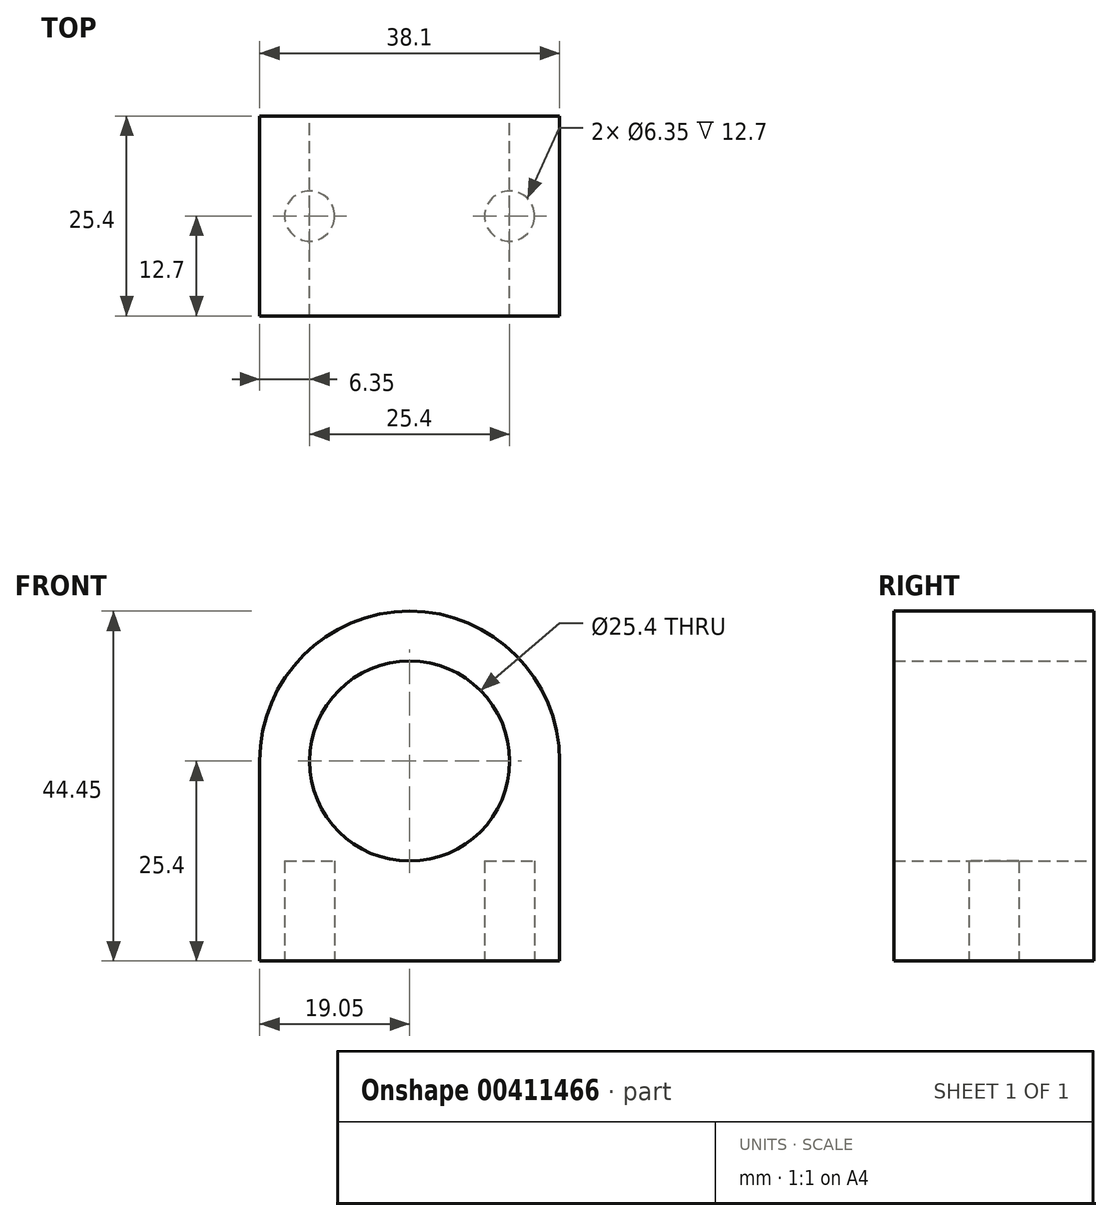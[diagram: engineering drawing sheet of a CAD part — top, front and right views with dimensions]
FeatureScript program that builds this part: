
annotation { "Feature Type Name" : "Feature", "Feature Type Description" : "" }
export const myFeature = defineFeature(function(context is Context, id is Id, definition is map)
    precondition{}
    {
        {
            var Q0;
            Q0=qCreatedBy(makeId("Front.planeOp"),FACE);
            var sketch = newSketch(context, id + "F0", { "sketchPlane" : qUnion([Q0])});
            skLineSegment(sketch, "E0.top", {"start": v(-19.05, -12.7) * mm, "end": v(19.05, -12.7) * mm});
            skLineSegment(sketch, "E0.left", {"start": v(-19.05, 12.7) * mm, "end": v(-19.05, -12.7) * mm});
            skLineSegment(sketch, "E0.right", {"start": v(19.05, 12.7) * mm, "end": v(19.05, -12.7) * mm});
            skArc(sketch, "E1", {"start": v(19.05, 12.7) * mm, "mid": v(0, 31.75) * mm, "end": v(-19.05, 12.7) * mm});
            skCircle(sketch, "E2", {"center": v(0, 12.7) * mm, "radius": 12.7 * mm});
            skSolve(sketch);
        }
        {
            var Q0;
            Q0=makeQuery(id+"F0.imprint","IMPRINT",FACE,{"disambiguationData":[TD([[makeQuery(id+"F0.imprint","IMPRINT",EDGE,{"derivedFrom":sQuery(id+"F0.wireOp",EDGE,"E0.top")}),1.0]])]});
            extrude(context, id + "F1", {"entities" : qUnion([Q0]), "depth" : 25.4 * mm});
        }
        {
            var Q0;
            Q0=makeQuery(id+"F1.opExtrude","SWEPT_FACE",FACE,{"disambiguationData":[OSD([sQuery(id+"F0.wireOp",EDGE,"E0.top")])]});
            var sketch = newSketch(context, id + "F2", { "sketchPlane" : qUnion([Q0])});
            skCircle(sketch, "E3", {"center": v(-12.7, 12.7) * mm, "radius": 3.18 * mm});
            skPoint(sketch, "E3.centerSnap0", {"position": v(-19.05, 12.7) * mm});
            skCircle(sketch, "E4", {"center": v(12.7, 12.7) * mm, "radius": 3.18 * mm});
            skSolve(sketch);
        }
        {
            var Q0;
            Q0=makeQuery(id+"F2.imprint","IMPRINT",FACE,{"disambiguationData":[TD([[makeQuery(id+"F2.imprint","IMPRINT",EDGE,{"derivedFrom":sQuery(id+"F2.wireOp",EDGE,"E3")}),1.0]])]});
            var Q1;
            Q1=makeQuery(id+"F2.imprint","IMPRINT",FACE,{"disambiguationData":[TD([[makeQuery(id+"F2.imprint","IMPRINT",EDGE,{"derivedFrom":sQuery(id+"F2.wireOp",EDGE,"E4")}),1.0]])]});
            extrude(context, id + "F3", {"entities" : qUnion([Q0, Q1]), "operationType" : NewBodyOperationType.REMOVE, "oppositeDirection" : true, "depth" : 12.7 * mm});
        }
    });
